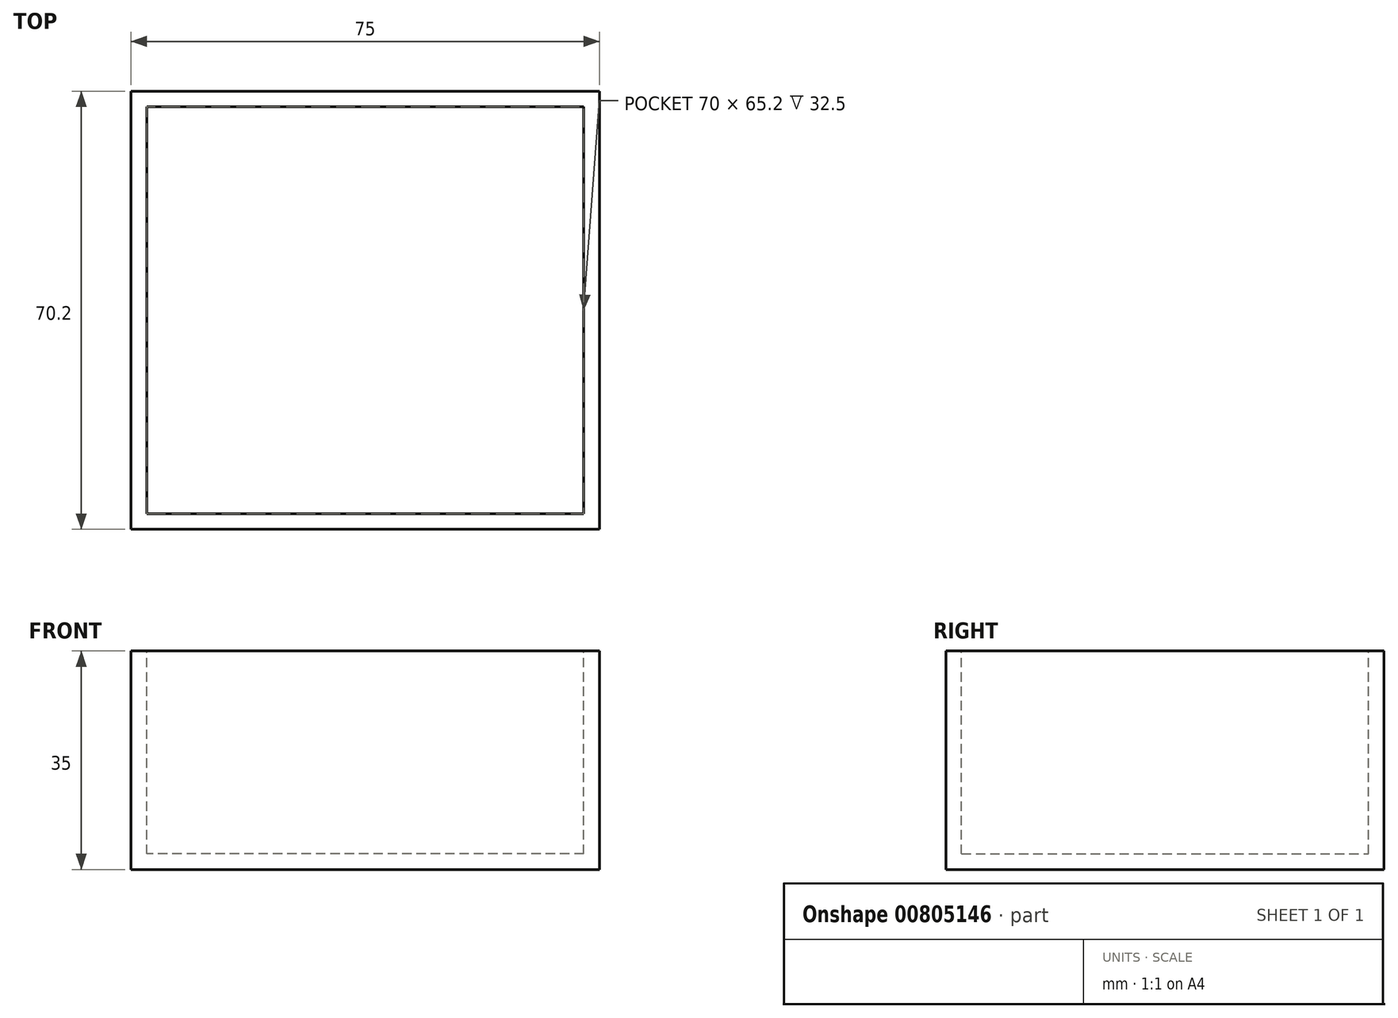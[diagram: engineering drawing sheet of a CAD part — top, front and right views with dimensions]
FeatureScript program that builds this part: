
annotation { "Feature Type Name" : "Feature", "Feature Type Description" : "" }
export const myFeature = defineFeature(function(context is Context, id is Id, definition is map)
    precondition{}
    {
        {
            var Q0;
            Q0=qCreatedBy(makeId("Front.planeOp"),FACE);
            var sketch = newSketch(context, id + "F0", { "sketchPlane" : qUnion([Q0])});
            skLineSegment(sketch, "E0.bottom", {"start": v(0, 0) * mm, "end": v(-75, 0) * mm});
            skLineSegment(sketch, "E0.top", {"start": v(0, 35) * mm, "end": v(-75, 35) * mm});
            skLineSegment(sketch, "E0.left", {"start": v(0, 0) * mm, "end": v(0, 35) * mm});
            skLineSegment(sketch, "E0.right", {"start": v(-75, 0) * mm, "end": v(-75, 35) * mm});
            skSolve(sketch);
        }
        {
            var Q0;
            Q0=qCreatedBy(makeId("Front.planeOp"),FACE);
            var sketch = newSketch(context, id + "F1", { "sketchPlane" : qUnion([Q0])});
            skSolve(sketch);
        }
        {
            var Q0;
            Q0 = qSketchRegion(id + "F1", true);
            var Q1;
            Q1=makeQuery(id+"F0.imprint","IMPRINT",FACE,{"disambiguationData":[TD([[makeQuery(id+"F0.imprint","IMPRINT",EDGE,{"derivedFrom":sQuery(id+"F0.wireOp",EDGE,"E0.bottom")}),-1.0]])]});
            extrude(context, id + "F2", {"entities" : qUnion([Q0, Q1]), "depth" : 70.2 * mm, "offsetDistance" : 25 * mm});
        }
        {
            var Q0;
            Q0=makeQuery(id+"F2.opExtrude","SWEPT_FACE",FACE,{"disambiguationData":[OSD([sQuery(id+"F0.wireOp",EDGE,"E0.top")])]});
            shell(context, id + "F3", {"entities" : qUnion([Q0]), "thickness" : 2.5 * mm});
        }
    });
